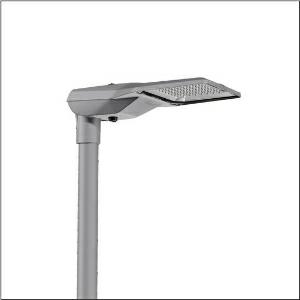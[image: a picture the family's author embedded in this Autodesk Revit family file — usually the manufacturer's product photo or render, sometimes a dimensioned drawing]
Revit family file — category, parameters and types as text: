
# Revit family: streetlight_sl_21_midi___st0_8a_5xe3c33t08lb_3015
name_source: partatom
category: Lighting Fixtures
units: mm (PartAtom-declared; Revit-internal decimal feet)

## family parameters
Cut with Voids When Loaded = No
Host = Face
Light Source = No
Part Type = Normal
Room Calculation Point = No
Round Connector Dimension = Use Diameter
Shared = No

## types (1)
- --- (1 x LED, 14340 lm, 99.6 W, 3000K)
    Apparent Load = 100 VA
    CIE Flux Codes = 38 75 97 100 100
    Color Rendering = 70
    Color Temperature = 3000K
    Default Elevation = 1800 mm
    Description = Streetlight SL 21 midi, mast luminaire, primary light control with lens, of PMMA, primary optical cover: cover, of toughened safety glass, transparent, light distribution: ST0.8a, light emission: direct distribution, primary light characteristic: asymmetric, installation type: side-entry, post-top, LED, High Power LED, rated luminous flux: 14.340lm, luminous efficacy: 144lm/W, light colour: 730, colour temperature: 3000K, control gear: D4i, control: overheat protection, constant luminous flux control, time-dependent luminous flux control, flexible luminous flux parameterisation, pre-setting: logarithmic dimming characteristic, mains connection: 230..240V, AC, 50/60Hz, start of lifetime: 100W, end of service life: 102W, reduction: 46W, luminaire housing, of diecast aluminium, powder-coated, Siteco® metallic grey (DB 702S), corrosivity category C5 mid according to DIN EN ISO 12944, please order mast flange separately, inclination adjustable: 0°, 5°, 10°, 15°, sealing non-destructively replaceable, multi-level sealing system, length: 644mm, width: 335mm, height: 110mm, mast flange for spigot size: 42mm (side-entry): 5XC10008XM4, 60/48mm (side-entry/post-top): 5XC10108XM2, 76/60mm (side-entry/post-top): 5XC10108XM1, mounting height: 4..8m, Smart Interface below and above, protection rating (complete): IP66, insulation class (complete): insulation class II (safety insulation), certification: CE, ENEC, ENEC+, VDE, impact resistance: IK10, permissible operating ambient temperature for outdoor applications: -40..+50°C, standard-compliant lighting for roads and squares, packaging unit: 1 piece

Light Distribution: ST0.8a
    Height = 111 mm
    Lamp = 1 x LED
    Lamp Light Flux = 14340 lm
    Lamp Power = 99.6 W
    Lamp count = 1
    Length = 644 mm
    Luminous efficacy = 144 lm/W
    Manufacturer = Siteco
    ModVariant = No
    Model = 5XE3C33T08LB
    Number of Poles = 1
    OnlyDefault = Yes
    Power Factor = 1
    Product Name = Streetlight SL 21 midi | ST0.8a
    Product group = mast luminaire | pylon top
    ProductGroupID = 6100
    Protection Class = Protection class II
    Protection Degree = IP 66
    RLX_Detail_Level = 1
    RLX_Emergency_Light_Flux = 0 lm
    RLX_Emergency_Type = 0
    RLX_Emergency_Type_DB = No
    RlxData = <blob elided: 27029 chars, md5=b955fd4a>
    Socket = socket
    Standby Power = 0 W
    System Light Flux = 14340 lm
    System Power = 100 W
    Type Comments = factory setting: luminous flux: 100 % | dim-lin: 254 | 1020 mA
    Type Image = l_1004304.jpg
    URL = http://relux.com
    VarID = @adj_031097
    Voltage = 0 V
    Weight = 0.00 kg
    Width = 336 mm

## geometry (parser evidence)
native form markers: Blend x4, Sweep x13
no freeform markers — native parametric forms only
